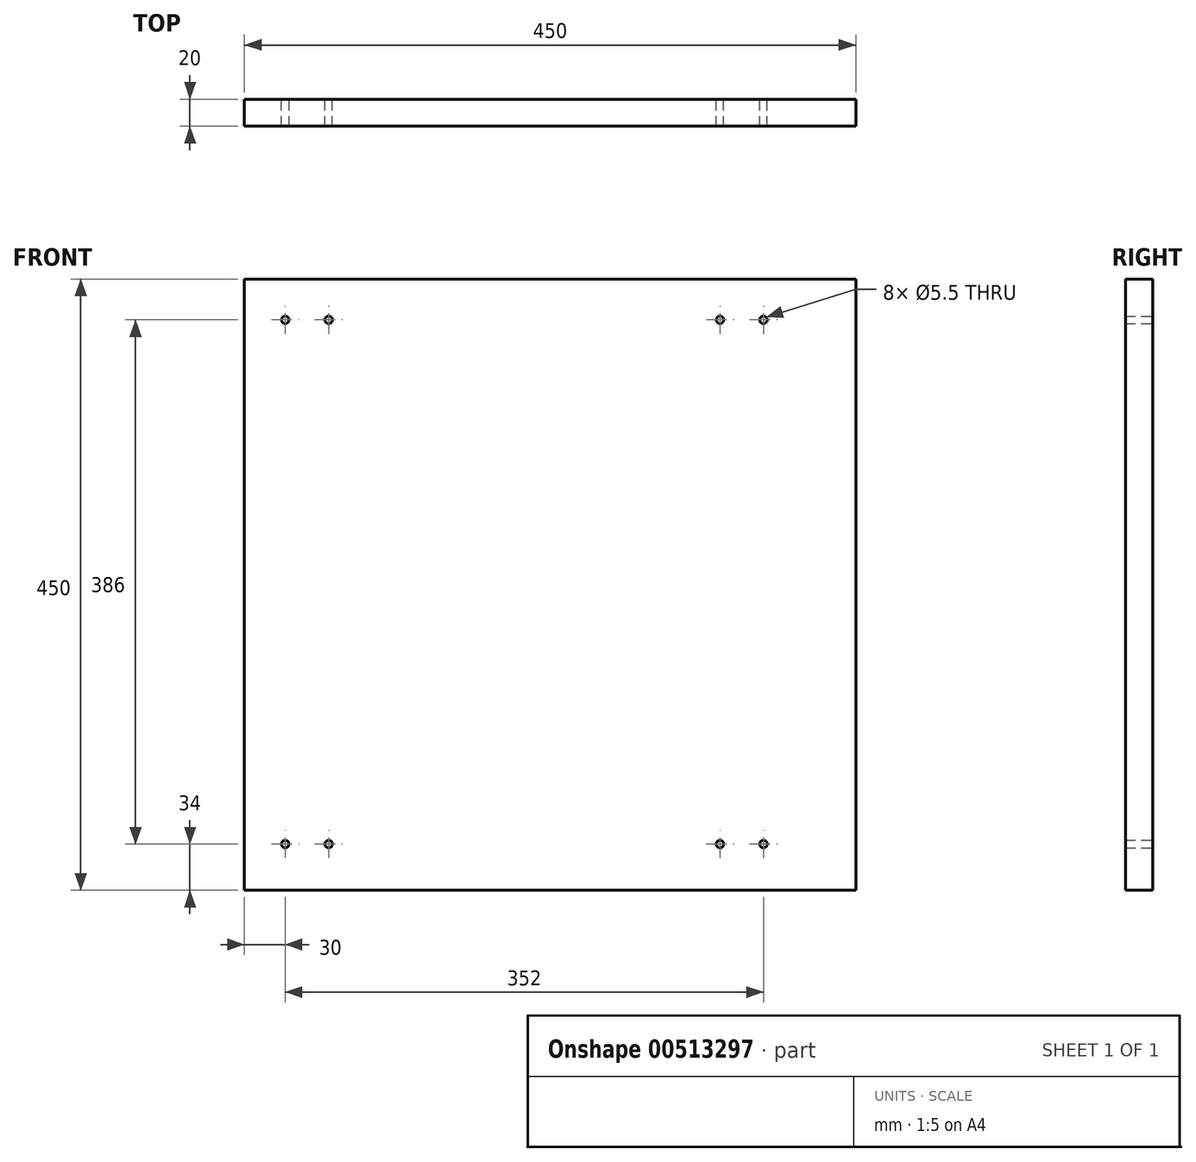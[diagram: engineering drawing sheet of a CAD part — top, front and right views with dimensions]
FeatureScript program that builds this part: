
annotation { "Feature Type Name" : "Feature", "Feature Type Description" : "" }
export const myFeature = defineFeature(function(context is Context, id is Id, definition is map)
    precondition{}
    {
        {
            var Q0;
            Q0=qCreatedBy(makeId("Front.planeOp"),FACE);
            var sketch = newSketch(context, id + "F0", { "sketchPlane" : qUnion([Q0])});
            skLineSegment(sketch, "E0.bottom", {"start": v(-225, 225) * mm, "end": v(225, 225) * mm});
            skLineSegment(sketch, "E0.top", {"start": v(-225, -225) * mm, "end": v(225, -225) * mm});
            skLineSegment(sketch, "E0.left", {"start": v(-225, 225) * mm, "end": v(-225, -225) * mm});
            skLineSegment(sketch, "E0.right", {"start": v(225, 225) * mm, "end": v(225, -225) * mm});
            skPoint(sketch, "E0.middle", {"position": v(0, 0) * mm});
            skCircle(sketch, "E1", {"center": v(-195, 195) * mm, "radius": 2.75 * mm});
            skCircle(sketch, "E2", {"center": v(-163, 195) * mm, "radius": 2.75 * mm});
            skCircle(sketch, "E3", {"center": v(125, 195) * mm, "radius": 2.75 * mm});
            skCircle(sketch, "E4", {"center": v(157, 195) * mm, "radius": 2.75 * mm});
            skCircle(sketch, "E5", {"center": v(-195, -191) * mm, "radius": 2.75 * mm});
            skCircle(sketch, "E6", {"center": v(-163, -191) * mm, "radius": 2.75 * mm});
            skCircle(sketch, "E7", {"center": v(125, -191) * mm, "radius": 2.75 * mm});
            skCircle(sketch, "E8", {"center": v(157, -191) * mm, "radius": 2.75 * mm});
            skSolve(sketch);
        }
        {
            var Q0;
            Q0 = qSketchRegion(id + "F0", true);
            extrude(context, id + "F1", {"entities" : qUnion([Q0]), "depth" : 20 * mm, "offsetDistance" : 25 * mm});
        }
    });
